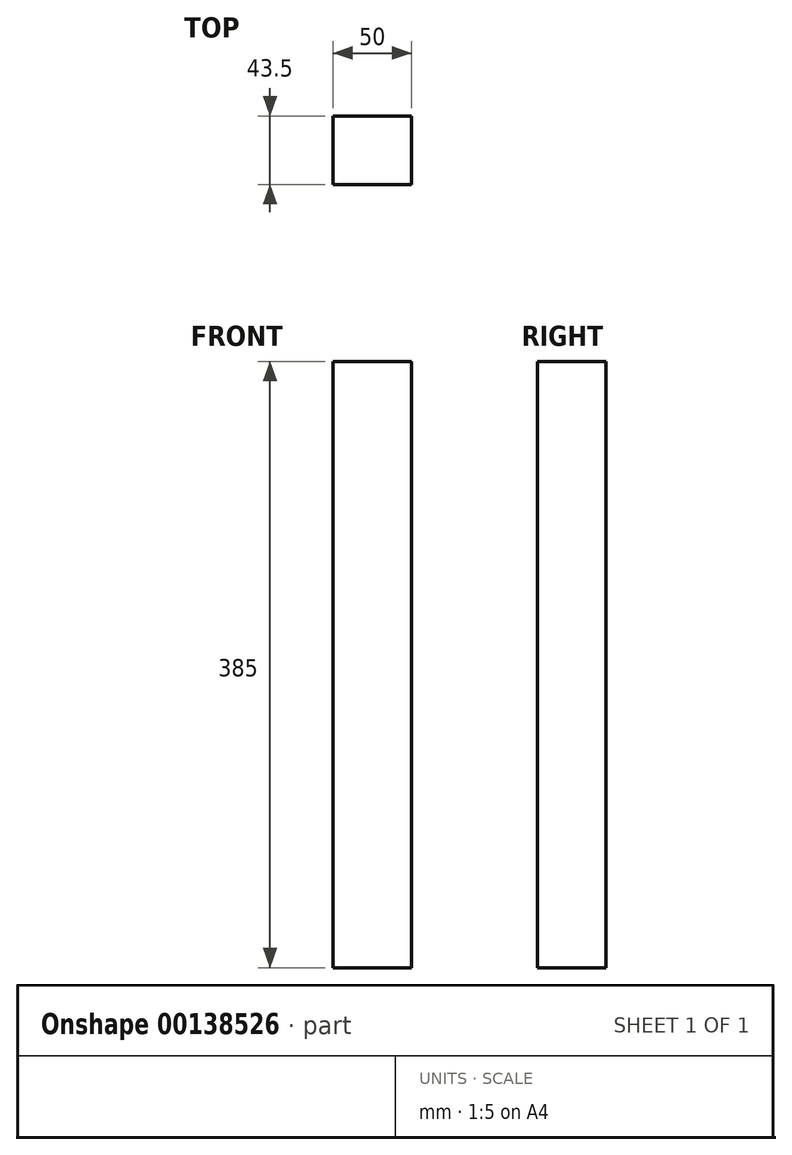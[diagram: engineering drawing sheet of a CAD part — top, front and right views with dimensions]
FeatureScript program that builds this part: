
annotation { "Feature Type Name" : "Feature", "Feature Type Description" : "" }
export const myFeature = defineFeature(function(context is Context, id is Id, definition is map)
    precondition{}
    {
        {
            var Q0;
            Q0=qCreatedBy(makeId("Top.planeOp"),FACE);
            var sketch = newSketch(context, id + "F0", { "sketchPlane" : qUnion([Q0])});
            skLineSegment(sketch, "E0.bottom", {"start": v(-25, -21.75) * mm, "end": v(25, -21.75) * mm});
            skLineSegment(sketch, "E0.top", {"start": v(-25, 21.75) * mm, "end": v(25, 21.75) * mm});
            skLineSegment(sketch, "E0.left", {"start": v(-25, -21.75) * mm, "end": v(-25, 21.75) * mm});
            skLineSegment(sketch, "E0.right", {"start": v(25, -21.75) * mm, "end": v(25, 21.75) * mm});
            skPoint(sketch, "E0.middle", {"position": v(0, 0) * mm});
            skSolve(sketch);
        }
        {
            var Q0;
            Q0=makeQuery(id+"F0.imprint","IMPRINT",FACE,{"disambiguationData":[TD([[makeQuery(id+"F0.imprint","IMPRINT",EDGE,{"derivedFrom":sQuery(id+"F0.wireOp",EDGE,"E0.bottom")}),1.0]])]});
            extrude(context, id + "F1", {"entities" : qUnion([Q0]), "depth" : 385 * mm});
        }
    });
